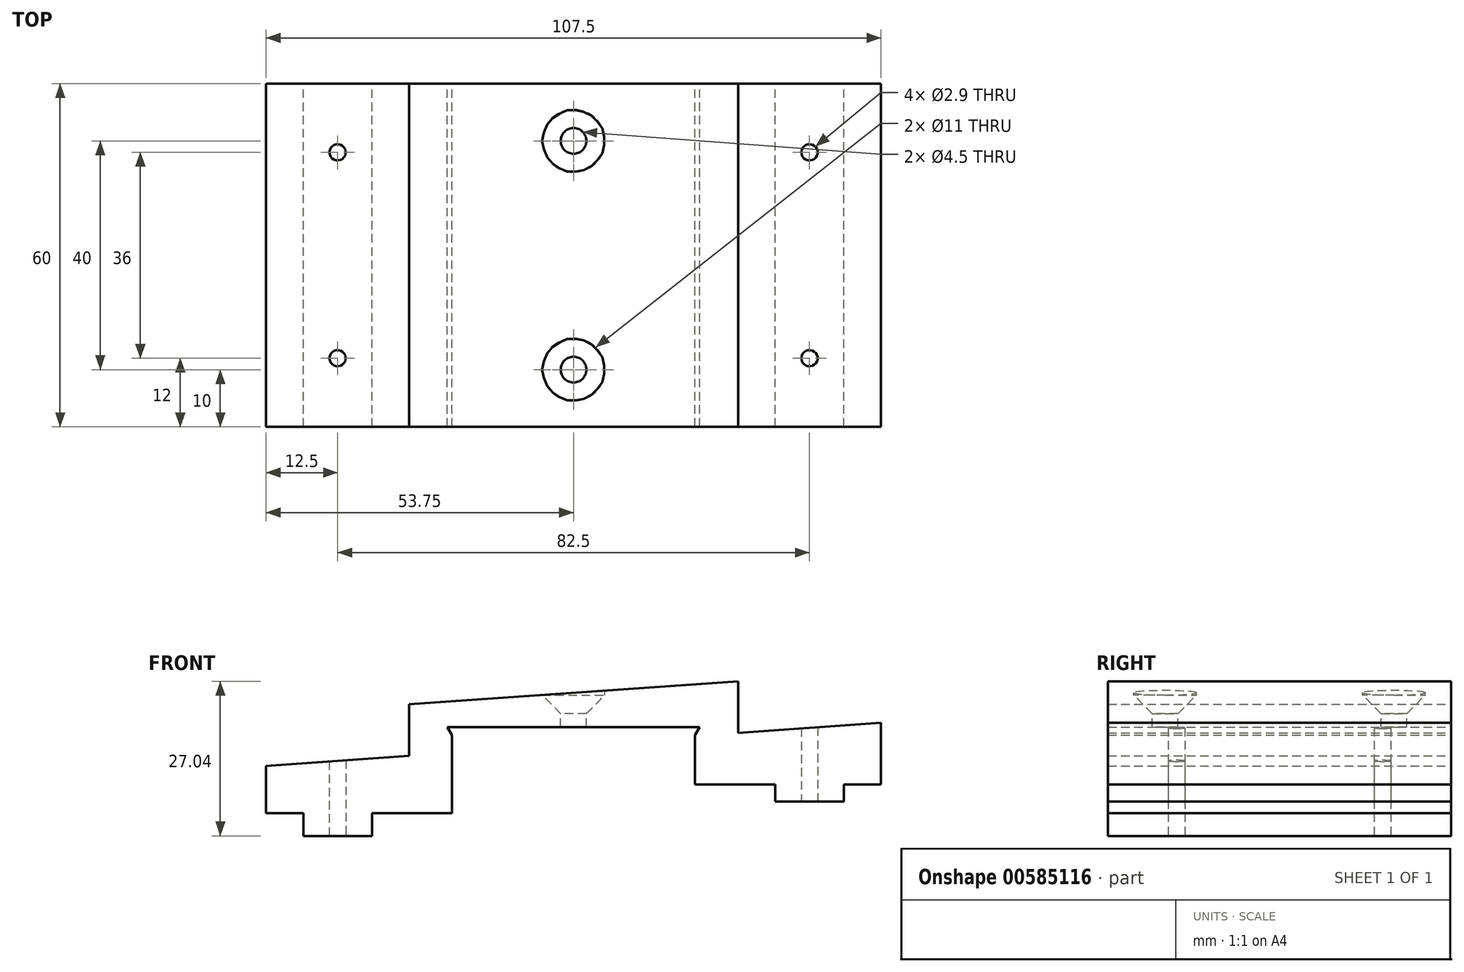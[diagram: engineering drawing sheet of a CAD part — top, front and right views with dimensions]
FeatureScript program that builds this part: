
annotation { "Feature Type Name" : "Feature", "Feature Type Description" : "" }
export const myFeature = defineFeature(function(context is Context, id is Id, definition is map)
    precondition{}
    {
        {
            var Q0;
            Q0=qCreatedBy(makeId("Front.planeOp"),FACE);
            var sketch = newSketch(context, id + "F0", { "sketchPlane" : qUnion([Q0])});
            skLineSegment(sketch, "E0", {"start": v(-43.3, 0) * mm, "end": v(0.8, 0) * mm});
            skLineSegment(sketch, "E1", {"start": v(0, -1.39) * mm, "end": v(0, -10.02) * mm});
            skLineSegment(sketch, "E2", {"start": v(0, -10.02) * mm, "end": v(32.5, -10.02) * mm});
            skLineSegment(sketch, "E3", {"start": v(32.5, -10.02) * mm, "end": v(32.5, 0.73) * mm});
            skLineSegment(sketch, "E4", {"start": v(32.5, 0.73) * mm, "end": v(7.5, -1.02) * mm});
            skLineSegment(sketch, "E5", {"start": v(7.5, -1.02) * mm, "end": v(7.5, 8) * mm});
            skLineSegment(sketch, "E6", {"start": v(7.5, 8) * mm, "end": v(-50, 3.98) * mm});
            skLineSegment(sketch, "E7", {"start": v(-50, 3.98) * mm, "end": v(-50, -5.04) * mm});
            skLineSegment(sketch, "E8", {"start": v(-50, -5.04) * mm, "end": v(-75, -6.8) * mm});
            skLineSegment(sketch, "E9", {"start": v(-75, -6.8) * mm, "end": v(-75, -15.04) * mm});
            skLineSegment(sketch, "E10", {"start": v(-75, -15.04) * mm, "end": v(-42.5, -15.04) * mm});
            skLineSegment(sketch, "E11", {"start": v(-42.5, -15.04) * mm, "end": v(-42.5, -1.39) * mm});
            skLineSegment(sketch, "E12", {"start": v(-43.3, 0) * mm, "end": v(-42.5, -1.39) * mm});
            skLineSegment(sketch, "E13", {"start": v(0, -1.39) * mm, "end": v(0.8, 0) * mm});
            skSolve(sketch);
        }
        {
            var Q0;
            Q0 = qSketchRegion(id + "F0", true);
            extrude(context, id + "F1", {"entities" : qUnion([Q0]), "depth" : 60 * mm, "offsetDistance" : 25 * mm});
        }
        {
            var Q0;
            Q0=qCreatedBy(makeId("Top.planeOp"),FACE);
            var Q1;
            Q1=makeQuery(id+"F1.opExtrude","CAP_VERTEX",VERTEX,{"disambiguationData":[OSD([sQuery(id+"F0.wireOp",EDGE,"E5"),sQuery(id+"F0.wireOp",EDGE,"E6")])],"isStart":false});
            cPlane(context, id + "F2", {"entities" : qUnion([Q0, Q1]), "cplaneType" : CPlaneType.PLANE_POINT, "offset" : 25 * mm, "width" : 150 * mm, "height" : 150 * mm});
        }
        {
            var Q0;
            Q0=qCreatedBy(id+"F2.planeOp",FACE);
            var sketch = newSketch(context, id + "F3", { "sketchPlane" : qUnion([Q0])});
            skLineSegment(sketch, "E14", {"start": v(-21.25, -60) * mm, "end": v(-21.25, -50) * mm});
            skLineSegment(sketch, "E15", {"start": v(-21.25, -50) * mm, "end": v(-21.25, -10) * mm});
            skLineSegment(sketch, "E16", {"start": v(-21.25, -10) * mm, "end": v(-21.25, 0) * mm});
            skPoint(sketch, "E17", {"position": v(-21.25, -10) * mm});
            skPoint(sketch, "E18", {"position": v(-21.25, -50) * mm});
            skSolve(sketch);
        }
        {
            var Q0;
            Q0=sQuery(id+"F3.wireOp",VERTEX,"E17");
            var Q1;
            Q1=sQuery(id+"F3.wireOp",VERTEX,"E18");
            var Q2;
            Q2=makeQuery(id+"F1.opExtrude","SWEPT_BODY",BODY,{"disambiguationData":[OSD([sQuery(id+"F0.wireOp",EDGE,"E0"),sQuery(id+"F0.wireOp",EDGE,"E1"),sQuery(id+"F0.wireOp",EDGE,"E2"),sQuery(id+"F0.wireOp",EDGE,"E3"),sQuery(id+"F0.wireOp",EDGE,"E4"),sQuery(id+"F0.wireOp",EDGE,"E5"),sQuery(id+"F0.wireOp",EDGE,"E6"),sQuery(id+"F0.wireOp",EDGE,"E7"),sQuery(id+"F0.wireOp",EDGE,"E8"),sQuery(id+"F0.wireOp",EDGE,"E9"),sQuery(id+"F0.wireOp",EDGE,"E10"),sQuery(id+"F0.wireOp",EDGE,"E11")])]});
            hole(context, id + "F4", {"style" : HoleStyle.C_SINK, "endStyle" : HoleEndStyle.THROUGH, "holeDiameter" : 4.5 * mm, "cSinkDiameter" : 11 * mm, "cSinkAngle" : 90 * degree, "majorDiameter" : 5 * mm, "isTappedThrough" : true, "tappedDepth" : 12 * mm, "tapClearance" : 3, "locations" : qUnion([Q0, Q1]), "scope" : qUnion([Q2])});
        }
        {
            var Q0;
            Q0=makeQuery(id+"F1.opExtrude","SWEPT_FACE",FACE,{"disambiguationData":[OSD([sQuery(id+"F0.wireOp",EDGE,"E10")])]});
            var sketch = newSketch(context, id + "F5", { "sketchPlane" : qUnion([Q0])});
            skLineSegment(sketch, "E19.top", {"start": v(-68.5, 0) * mm, "end": v(-56.5, 0) * mm});
            skLineSegment(sketch, "E19.left", {"start": v(-68.5, 60) * mm, "end": v(-68.5, 0) * mm});
            skLineSegment(sketch, "E19.right", {"start": v(-56.5, 60) * mm, "end": v(-56.5, 0) * mm});
            skPoint(sketch, "E20.0", {"position": v(-62.5, 60) * mm});
            skLineSegment(sketch, "E21", {"start": v(-68.5, 60) * mm, "end": v(-62.5, 60) * mm});
            skLineSegment(sketch, "E22", {"start": v(-62.5, 60) * mm, "end": v(-56.5, 60) * mm});
            skSolve(sketch);
        }
        {
            var Q0;
            Q0 = qSketchRegion(id + "F5", true);
            extrude(context, id + "F6", {"entities" : qUnion([Q0]), "operationType" : NewBodyOperationType.ADD, "depth" : 4 * mm, "offsetDistance" : 25 * mm});
        }
        {
            var Q0;
            Q0=makeQuery(id+"F1.opExtrude","SWEPT_FACE",FACE,{"disambiguationData":[OSD([sQuery(id+"F0.wireOp",EDGE,"E2")])]});
            var sketch = newSketch(context, id + "F7", { "sketchPlane" : qUnion([Q0])});
            skLineSegment(sketch, "E23.top", {"start": v(14, 0) * mm, "end": v(26, 0) * mm});
            skLineSegment(sketch, "E23.left", {"start": v(14, 60) * mm, "end": v(14, 0) * mm});
            skLineSegment(sketch, "E23.right", {"start": v(26, 60) * mm, "end": v(26, 0) * mm});
            skLineSegment(sketch, "E24", {"start": v(14, 60) * mm, "end": v(20, 60) * mm});
            skLineSegment(sketch, "E25", {"start": v(20, 60) * mm, "end": v(26, 60) * mm});
            skPoint(sketch, "E26.0", {"position": v(20, 60) * mm});
            skSolve(sketch);
        }
        {
            var Q0;
            Q0 = qSketchRegion(id + "F7", true);
            extrude(context, id + "F8", {"entities" : qUnion([Q0]), "operationType" : NewBodyOperationType.ADD, "depth" : 3 * mm, "offsetDistance" : 25 * mm});
        }
        {
            var Q0;
            Q0=makeQuery(id+"F6.opExtrude","CAP_FACE",FACE,{"disambiguationData":[OSD([sQuery(id+"F5.wireOp",EDGE,"E19.top"),sQuery(id+"F5.wireOp",EDGE,"E19.left"),sQuery(id+"F5.wireOp",EDGE,"E19.right"),sQuery(id+"F5.wireOp",EDGE,"E21"),sQuery(id+"F5.wireOp",EDGE,"E22")])],"isStart":false});
            var sketch = newSketch(context, id + "F9", { "sketchPlane" : qUnion([Q0])});
            skLineSegment(sketch, "E27", {"start": v(-62.5, 60) * mm, "end": v(-62.5, 48) * mm});
            skLineSegment(sketch, "E28", {"start": v(-62.5, 48) * mm, "end": v(-62.5, 12) * mm});
            skLineSegment(sketch, "E29", {"start": v(-62.5, 12) * mm, "end": v(-62.5, 0) * mm});
            skPoint(sketch, "E30", {"position": v(-62.5, 48) * mm});
            skPoint(sketch, "E31", {"position": v(-62.5, 12) * mm});
            skPoint(sketch, "E32", {"position": v(20, 48) * mm});
            skPoint(sketch, "E33", {"position": v(20, 12) * mm});
            skLineSegment(sketch, "E34", {"start": v(20, 48) * mm, "end": v(20, 12) * mm});
            skSolve(sketch);
        }
        {
            var Q0;
            Q0=sQuery(id+"F9.wireOp",VERTEX,"E32");
            var Q1;
            Q1=sQuery(id+"F9.wireOp",VERTEX,"E33");
            var Q2;
            Q2=sQuery(id+"F9.wireOp",VERTEX,"E30");
            var Q3;
            Q3=sQuery(id+"F9.wireOp",VERTEX,"E31");
            var Q4;
            Q4=makeQuery(id+"F1.opExtrude","SWEPT_BODY",BODY,{"disambiguationData":[OSD([sQuery(id+"F0.wireOp",EDGE,"E0"),sQuery(id+"F0.wireOp",EDGE,"E1"),sQuery(id+"F0.wireOp",EDGE,"E2"),sQuery(id+"F0.wireOp",EDGE,"E3"),sQuery(id+"F0.wireOp",EDGE,"E4"),sQuery(id+"F0.wireOp",EDGE,"E5"),sQuery(id+"F0.wireOp",EDGE,"E6"),sQuery(id+"F0.wireOp",EDGE,"E7"),sQuery(id+"F0.wireOp",EDGE,"E8"),sQuery(id+"F0.wireOp",EDGE,"E9"),sQuery(id+"F0.wireOp",EDGE,"E10"),sQuery(id+"F0.wireOp",EDGE,"E11")])]});
            hole(context, id + "F10", {"style" : HoleStyle.SIMPLE, "endStyle" : HoleEndStyle.THROUGH, "holeDiameter" : 2.9 * mm, "majorDiameter" : 5 * mm, "isTappedThrough" : true, "tappedDepth" : 12 * mm, "tapClearance" : 3, "locations" : qUnion([Q0, Q1, Q2, Q3]), "scope" : qUnion([Q4])});
        }
    });
